# Revit family: EV4R-Round Trim
name_source: partatom
category: Lighting Fixtures
units: mm (PartAtom-declared; Revit-internal decimal feet)

## family parameters
Cut with Voids When Loaded = No
Host = Face
Light Source = No
OmniClass Number = 23.80.70.11
OmniClass Title = Luminaries for Internal Lighting
Part Type = Normal
Room Calculation Point = No
Round Connector Dimension = Use Diameter
Shared = No

## types (2) — shared parameters
Apparent Load = 1 VA
Default Elevation = 4' - 0"
Description = Recessed Ceiling Mount LED Emergency Light
Housing = Aluminum
Input Power = 1 W
Lamp = 4 LEDs
Load Classification = Lighting
Manufacturer = Dual Lite
Model = EV4R-Round
Power Factor = 1
URL = https://www.currentlighting.com
Voltage = 120 V
Wattage Comments = 1 watt each for 88 lumens per LED

## per-type parameters (varying)
| type | Angle | Trim Plate | zz Angle 1 |
| White | 110.00° | Paint - White | 105.00° |
| Black | 80.00° | Paint - Black | 80.00° |

## geometry (parser evidence)
native form markers: Blend x3, Sweep x7
no freeform markers — native parametric forms only
